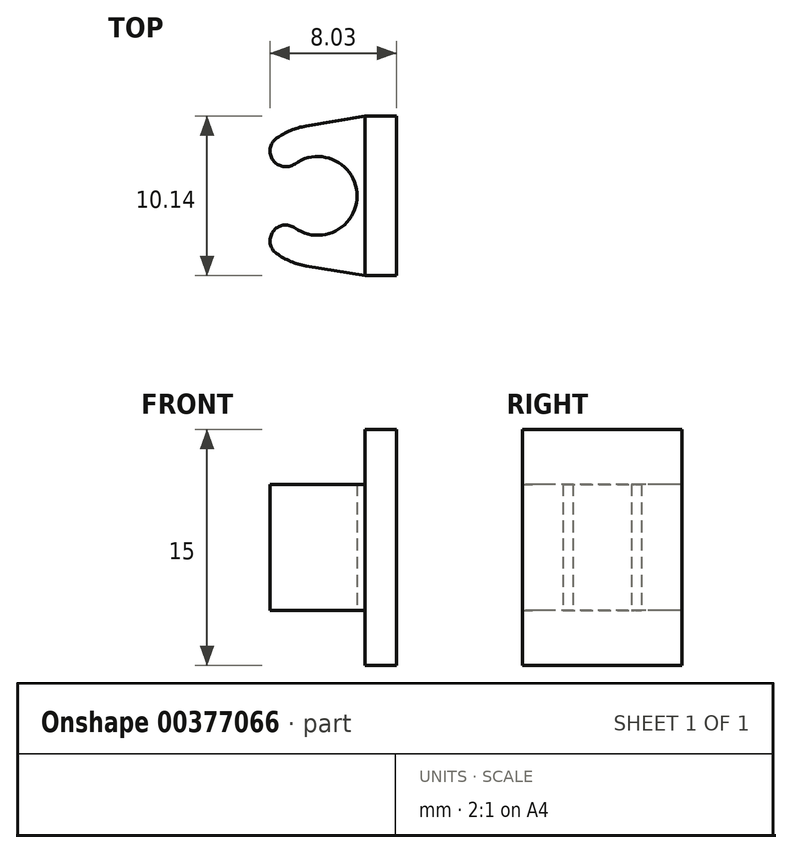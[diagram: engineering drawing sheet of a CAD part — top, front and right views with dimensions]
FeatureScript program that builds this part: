
annotation { "Feature Type Name" : "Feature", "Feature Type Description" : "" }
export const myFeature = defineFeature(function(context is Context, id is Id, definition is map)
    precondition{}
    {
        {
            var Q0;
            Q0=qCreatedBy(makeId("Top.planeOp"),FACE);
            var sketch = newSketch(context, id + "F0", { "sketchPlane" : qUnion([Q0])});
            skArc(sketch, "E0", {"start": v(-4.45, -2.04) * mm, "mid": v(-0.5, 0) * mm, "end": v(-4.45, 2.04) * mm});
            skArc(sketch, "E1.0", {"start": v(-3.75, 4.44) * mm, "mid": v(-4.72, 4.16) * mm, "end": v(-5.61, 3.66) * mm});
            skLineSegment(sketch, "E2", {"start": v(0, 5.07) * mm, "end": v(-3.75, 4.44) * mm});
            skLineSegment(sketch, "E3", {"start": v(0, -5.07) * mm, "end": v(-3.75, -4.44) * mm});
            skPoint(sketch, "E4.right.end.orphan", {"position": v(-0.51, 1.75) * mm});
            skPoint(sketch, "E5.orphan", {"position": v(-1.71, -1.27) * mm});
            skArc(sketch, "E6.trimOffspring", {"start": v(-5.61, -3.66) * mm, "mid": v(-4.72, -4.16) * mm, "end": v(-3.75, -4.44) * mm});
            skPoint(sketch, "E7.visualSharp", {"position": v(-4.45, 2.04) * mm});
            skArc(sketch, "E7.filletArc", {"start": v(-5.61, 3.66) * mm, "mid": v(-5.85, 2.27) * mm, "end": v(-4.45, 2.04) * mm});
            skArc(sketch, "E8.filletArc", {"start": v(-4.45, -2.04) * mm, "mid": v(-5.85, -2.27) * mm, "end": v(-5.61, -3.66) * mm});
            skLineSegment(sketch, "E9", {"start": v(-5.03, 2.85) * mm, "end": v(-5.03, -2.85) * mm, "construction": true});
            skLineSegment(sketch, "E10", {"start": v(0, 5.07) * mm, "end": v(0, -5.07) * mm});
            skSolve(sketch);
        }
        {
            var Q0;
            Q0=qSketchRegion(id+"F0",true);
            extrude(context, id + "F1", {"entities" : qUnion([Q0]), "depth" : 8 * mm});
        }
        {
            var Q0;
            Q0=makeQuery(id+"F1.opExtrude","SWEPT_FACE",FACE,{"disambiguationData":[OSD([sQuery(id+"F0.wireOp",EDGE,"E10")])]});
            var sketch = newSketch(context, id + "F2", { "sketchPlane" : qUnion([Q0])});
            skLineSegment(sketch, "E11.bottom", {"start": v(5.07, 11.5) * mm, "end": v(-5.07, 11.5) * mm});
            skLineSegment(sketch, "E11.top", {"start": v(5.07, -3.5) * mm, "end": v(-5.07, -3.5) * mm});
            skLineSegment(sketch, "E11.left", {"start": v(5.07, 11.5) * mm, "end": v(5.07, -3.5) * mm});
            skLineSegment(sketch, "E11.right", {"start": v(-5.07, 11.5) * mm, "end": v(-5.07, -3.5) * mm});
            skPoint(sketch, "E11.middle", {"position": v(0, 4) * mm});
            skPoint(sketch, "E11.middle.positionSnap0", {"position": v(-5.07, 4) * mm});
            skPoint(sketch, "E11.centerSnap0", {"position": v(-5.07, 4) * mm});
            skSolve(sketch);
        }
        {
            var Q0;
            Q0 = qSketchRegion(id + "F2", true);
            extrude(context, id + "F3", {"entities" : qUnion([Q0]), "operationType" : NewBodyOperationType.ADD, "depth" : 2 * mm});
        }
    });
